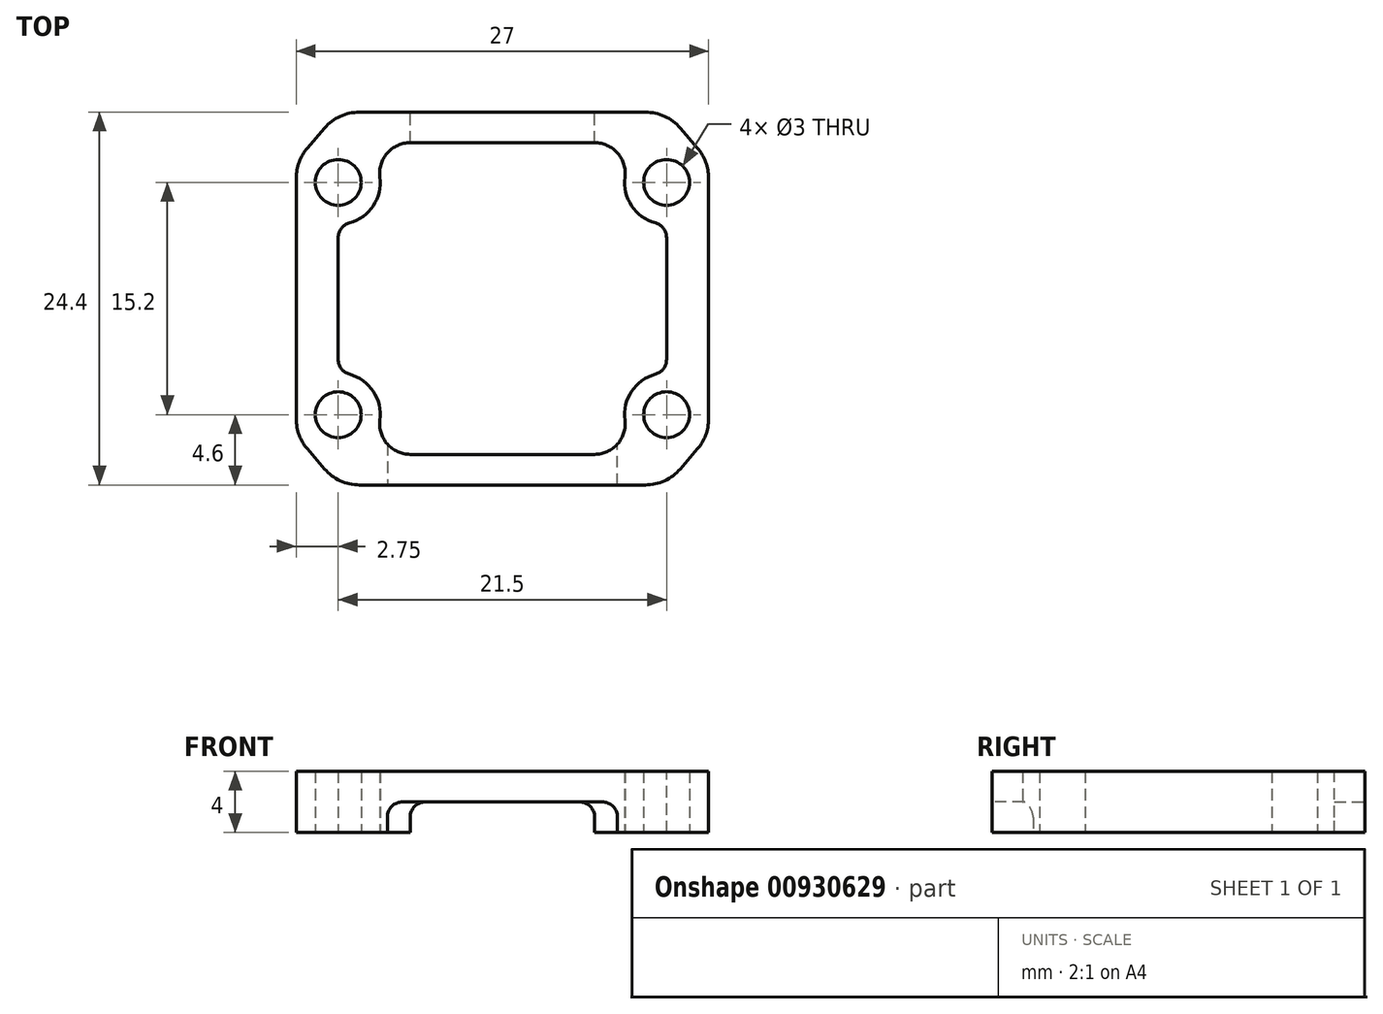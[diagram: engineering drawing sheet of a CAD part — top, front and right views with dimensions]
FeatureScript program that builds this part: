
annotation { "Feature Type Name" : "Feature", "Feature Type Description" : "" }
export const myFeature = defineFeature(function(context is Context, id is Id, definition is map)
    precondition{}
    {
        {
            var Q0;
            Q0=qCreatedBy(makeId("Top.planeOp"),FACE);
            var sketch = newSketch(context, id + "F0", { "sketchPlane" : qUnion([Q0])});
            skCircle(sketch, "E0", {"center": v(0, 0) * mm, "radius": 1.5 * mm});
            skCircle(sketch, "E1", {"center": v(0, 15.2) * mm, "radius": 1.5 * mm});
            skCircle(sketch, "E2", {"center": v(21.5, 15.2) * mm, "radius": 1.5 * mm});
            skCircle(sketch, "E3", {"center": v(21.5, 0) * mm, "radius": 1.5 * mm});
            skLineSegment(sketch, "E4", {"start": v(-2.75, 16.6) * mm, "end": v(-2.75, -1.4) * mm});
            skLineSegment(sketch, "E5", {"start": v(24.25, 16.6) * mm, "end": v(24.25, -1.4) * mm});
            skLineSegment(sketch, "E6", {"start": v(0.9, -2.6) * mm, "end": v(20.6, -2.6) * mm});
            skLineSegment(sketch, "E7", {"start": v(0.9, 17.8) * mm, "end": v(20.6, 17.8) * mm});
            skArc(sketch, "E8", {"start": v(0, 12.45) * mm, "mid": v(2.71, 14.75) * mm, "end": v(0.9, 17.8) * mm});
            skLineSegment(sketch, "E9", {"start": v(0, 12.45) * mm, "end": v(0, 2.75) * mm});
            skLineSegment(sketch, "E10", {"start": v(0, 19.8) * mm, "end": v(21.5, 19.8) * mm});
            skLineSegment(sketch, "E11", {"start": v(-2.75, 16.6) * mm, "end": v(0, 19.8) * mm});
            skLineSegment(sketch, "E12", {"start": v(21.5, 12.45) * mm, "end": v(21.5, 2.75) * mm});
            skArc(sketch, "E13", {"start": v(20.6, 17.8) * mm, "mid": v(18.79, 14.75) * mm, "end": v(21.5, 12.45) * mm});
            skLineSegment(sketch, "E14", {"start": v(21.5, 19.8) * mm, "end": v(24.25, 16.6) * mm});
            skLineSegment(sketch, "E15", {"start": v(0, -4.6) * mm, "end": v(21.5, -4.6) * mm});
            skLineSegment(sketch, "E16", {"start": v(21.5, -4.6) * mm, "end": v(24.25, -1.4) * mm});
            skLineSegment(sketch, "E17", {"start": v(-2.75, -1.4) * mm, "end": v(0, -4.6) * mm});
            skArc(sketch, "E18", {"start": v(0.9, -2.6) * mm, "mid": v(2.71, 0.45) * mm, "end": v(0, 2.75) * mm});
            skArc(sketch, "E19", {"start": v(21.5, 2.75) * mm, "mid": v(18.79, 0.45) * mm, "end": v(20.6, -2.6) * mm});
            skSolve(sketch);
        }
        {
            var Q0;
            Q0=qSketchRegion(id+"F0",true);
            extrude(context, id + "F1", {"entities" : qUnion([Q0]), "depth" : 4 * mm, "offsetDistance" : 25 * mm});
        }
        {
            var Q0;
            Q0=makeQuery(id+"F1.opExtrude","SWEPT_EDGE",EDGE,{"disambiguationData":[OSD([sQuery(id+"F0.wireOp",EDGE,"E7"),sQuery(id+"F0.wireOp",EDGE,"E8")])]});
            var Q1;
            Q1=makeQuery(id+"F1.opExtrude","SWEPT_EDGE",EDGE,{"disambiguationData":[OSD([sQuery(id+"F0.wireOp",EDGE,"E7"),sQuery(id+"F0.wireOp",EDGE,"E13")])]});
            var Q2;
            Q2=makeQuery(id+"F1.opExtrude","SWEPT_EDGE",EDGE,{"disambiguationData":[OSD([sQuery(id+"F0.wireOp",EDGE,"E6"),sQuery(id+"F0.wireOp",EDGE,"E18")])]});
            var Q3;
            Q3=makeQuery(id+"F1.opExtrude","SWEPT_EDGE",EDGE,{"disambiguationData":[OSD([sQuery(id+"F0.wireOp",EDGE,"E6"),sQuery(id+"F0.wireOp",EDGE,"E19")])]});
            fillet(context, id + "F2", {"entities" : qUnion([Q0, Q1, Q2, Q3]), "radius" : 2 * mm, "tangentPropagation" : true, "allowEdgeOverflow" : false});
        }
        {
            var Q0;
            Q0=makeQuery(id+"F1.opExtrude","SWEPT_EDGE",EDGE,{"disambiguationData":[OSD([sQuery(id+"F0.wireOp",EDGE,"E8"),sQuery(id+"F0.wireOp",EDGE,"E9")])]});
            var Q1;
            Q1=makeQuery(id+"F1.opExtrude","SWEPT_EDGE",EDGE,{"disambiguationData":[OSD([sQuery(id+"F0.wireOp",EDGE,"E9"),sQuery(id+"F0.wireOp",EDGE,"E18")])]});
            var Q2;
            Q2=makeQuery(id+"F1.opExtrude","SWEPT_EDGE",EDGE,{"disambiguationData":[OSD([sQuery(id+"F0.wireOp",EDGE,"E12"),sQuery(id+"F0.wireOp",EDGE,"E13")])]});
            var Q3;
            Q3=makeQuery(id+"F1.opExtrude","SWEPT_EDGE",EDGE,{"disambiguationData":[OSD([sQuery(id+"F0.wireOp",EDGE,"E12"),sQuery(id+"F0.wireOp",EDGE,"E19")])]});
            fillet(context, id + "F3", {"entities" : qUnion([Q0, Q1, Q2, Q3]), "radius" : 1 * mm, "tangentPropagation" : true, "allowEdgeOverflow" : false});
        }
        {
            var Q0;
            Q0=makeQuery(id+"F1.opExtrude","SWEPT_EDGE",EDGE,{"disambiguationData":[OSD([sQuery(id+"F0.wireOp",EDGE,"E15"),sQuery(id+"F0.wireOp",EDGE,"E17")])]});
            var Q1;
            Q1=makeQuery(id+"F1.opExtrude","SWEPT_EDGE",EDGE,{"disambiguationData":[OSD([sQuery(id+"F0.wireOp",EDGE,"E15"),sQuery(id+"F0.wireOp",EDGE,"E16")])]});
            var Q2;
            Q2=makeQuery(id+"F1.opExtrude","SWEPT_EDGE",EDGE,{"disambiguationData":[OSD([sQuery(id+"F0.wireOp",EDGE,"E5"),sQuery(id+"F0.wireOp",EDGE,"E16")])]});
            var Q3;
            Q3=makeQuery(id+"F1.opExtrude","SWEPT_EDGE",EDGE,{"disambiguationData":[OSD([sQuery(id+"F0.wireOp",EDGE,"E5"),sQuery(id+"F0.wireOp",EDGE,"E14")])]});
            var Q4;
            Q4=makeQuery(id+"F1.opExtrude","SWEPT_EDGE",EDGE,{"disambiguationData":[OSD([sQuery(id+"F0.wireOp",EDGE,"E10"),sQuery(id+"F0.wireOp",EDGE,"E14")])]});
            var Q5;
            Q5=makeQuery(id+"F1.opExtrude","SWEPT_EDGE",EDGE,{"disambiguationData":[OSD([sQuery(id+"F0.wireOp",EDGE,"E10"),sQuery(id+"F0.wireOp",EDGE,"E11")])]});
            var Q6;
            Q6=makeQuery(id+"F1.opExtrude","SWEPT_EDGE",EDGE,{"disambiguationData":[OSD([sQuery(id+"F0.wireOp",EDGE,"E4"),sQuery(id+"F0.wireOp",EDGE,"E11")])]});
            var Q7;
            Q7=makeQuery(id+"F1.opExtrude","SWEPT_EDGE",EDGE,{"disambiguationData":[OSD([sQuery(id+"F0.wireOp",EDGE,"E4"),sQuery(id+"F0.wireOp",EDGE,"E17")])]});
            fillet(context, id + "F4", {"entities" : qUnion([Q0, Q1, Q2, Q3, Q4, Q5, Q6, Q7]), "radius" : 3 * mm, "tangentPropagation" : true, "allowEdgeOverflow" : false});
        }
        {
            var Q0;
            Q0=makeQuery(id+"F1.opExtrude","CAP_FACE",FACE,{"disambiguationData":[OSD([sQuery(id+"F0.wireOp",EDGE,"E0"),sQuery(id+"F0.wireOp",EDGE,"E1"),sQuery(id+"F0.wireOp",EDGE,"E2"),sQuery(id+"F0.wireOp",EDGE,"E3"),sQuery(id+"F0.wireOp",EDGE,"E4"),sQuery(id+"F0.wireOp",EDGE,"E5"),sQuery(id+"F0.wireOp",EDGE,"E6"),sQuery(id+"F0.wireOp",EDGE,"E7"),sQuery(id+"F0.wireOp",EDGE,"E8"),sQuery(id+"F0.wireOp",EDGE,"E9"),sQuery(id+"F0.wireOp",EDGE,"E10"),sQuery(id+"F0.wireOp",EDGE,"E11"),sQuery(id+"F0.wireOp",EDGE,"E12"),sQuery(id+"F0.wireOp",EDGE,"E13"),sQuery(id+"F0.wireOp",EDGE,"E14"),sQuery(id+"F0.wireOp",EDGE,"E15"),sQuery(id+"F0.wireOp",EDGE,"E16"),sQuery(id+"F0.wireOp",EDGE,"E17"),sQuery(id+"F0.wireOp",EDGE,"E18"),sQuery(id+"F0.wireOp",EDGE,"E19")])],"isStart":true});
            var sketch = newSketch(context, id + "F5", { "sketchPlane" : qUnion([Q0])});
            skLineSegment(sketch, "E20.bottom", {"start": v(4.71, -17.8) * mm, "end": v(16.79, -17.8) * mm});
            skLineSegment(sketch, "E20.top", {"start": v(4.71, -19.8) * mm, "end": v(16.79, -19.8) * mm});
            skLineSegment(sketch, "E20.left", {"start": v(4.71, -17.8) * mm, "end": v(4.71, -19.8) * mm});
            skLineSegment(sketch, "E20.right", {"start": v(16.79, -17.8) * mm, "end": v(16.79, -19.8) * mm});
            skLineSegment(sketch, "E21", {"start": v(3.21, 1.92) * mm, "end": v(3.21, 4.6) * mm});
            skLineSegment(sketch, "E22", {"start": v(3.21, 4.6) * mm, "end": v(18.29, 4.6) * mm});
            skLineSegment(sketch, "E23", {"start": v(18.29, 4.6) * mm, "end": v(18.29, 1.92) * mm});
            skLineSegment(sketch, "E24", {"start": v(4.71, 2.6) * mm, "end": v(16.79, 2.6) * mm});
            skArc(sketch, "E25", {"start": v(4.71, 2.6) * mm, "mid": v(3.89, 2.42) * mm, "end": v(3.21, 1.92) * mm});
            skArc(sketch, "E26", {"start": v(18.29, 1.92) * mm, "mid": v(17.61, 2.42) * mm, "end": v(16.79, 2.6) * mm});
            skSolve(sketch);
        }
        {
            var Q0;
            Q0=qSketchRegion(id+"F5",true);
            extrude(context, id + "F6", {"entities" : qUnion([Q0]), "operationType" : NewBodyOperationType.REMOVE, "oppositeDirection" : true, "depth" : 2 * mm, "offsetDistance" : 25 * mm});
        }
        {
            var Q0;
            Q0=makeQuery(id+"F6.boolean.opBoolean","COPY",EDGE,{"derivedFrom":makeQuery(id+"F6.opExtrude","CAP_EDGE",EDGE,{"disambiguationData":[OSD([sQuery(id+"F5.wireOp",EDGE,"E20.left")])],"isStart":false})});
            var Q1;
            Q1=makeQuery(id+"F6.boolean.opBoolean","COPY",EDGE,{"derivedFrom":makeQuery(id+"F6.opExtrude","CAP_EDGE",EDGE,{"disambiguationData":[OSD([sQuery(id+"F5.wireOp",EDGE,"E20.right")])],"isStart":false})});
            var Q2;
            Q2=makeQuery(id+"F6.boolean.opBoolean","COPY",EDGE,{"derivedFrom":makeQuery(id+"F6.opExtrude","CAP_EDGE",EDGE,{"disambiguationData":[OSD([sQuery(id+"F5.wireOp",EDGE,"E23")])],"isStart":false})});
            var Q3;
            Q3=makeQuery(id+"F6.boolean.opBoolean","COPY",EDGE,{"derivedFrom":makeQuery(id+"F6.opExtrude","CAP_EDGE",EDGE,{"disambiguationData":[OSD([sQuery(id+"F5.wireOp",EDGE,"E21")])],"isStart":false})});
            fillet(context, id + "F7", {"entities" : qUnion([Q0, Q1, Q2, Q3]), "radius" : 1 * mm, "tangentPropagation" : true, "allowEdgeOverflow" : false});
        }
    });
